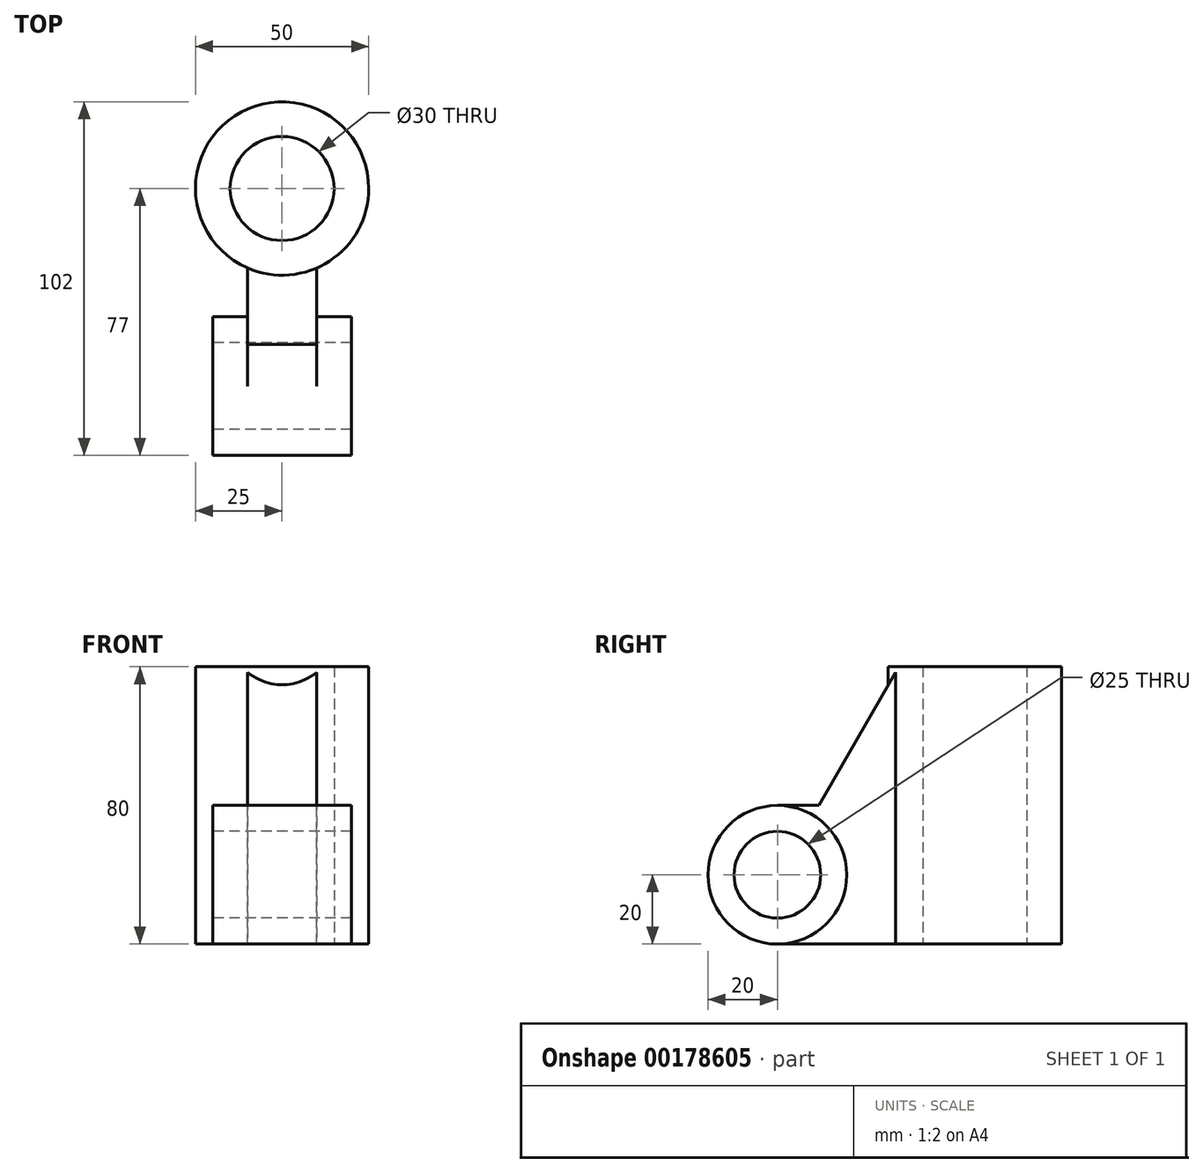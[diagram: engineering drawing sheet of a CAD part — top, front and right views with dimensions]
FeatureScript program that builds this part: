
annotation { "Feature Type Name" : "Feature", "Feature Type Description" : "" }
export const myFeature = defineFeature(function(context is Context, id is Id, definition is map)
    precondition{}
    {
        {
            var Q0;
            Q0=qCreatedBy(makeId("Top.planeOp"),FACE);
            var sketch = newSketch(context, id + "F0", { "sketchPlane" : qUnion([Q0])});
            skCircle(sketch, "E0", {"center": v(0, 0) * mm, "radius": 25 * mm});
            skCircle(sketch, "E1", {"center": v(0, 0) * mm, "radius": 15 * mm});
            skSolve(sketch);
        }
        {
            var Q0;
            Q0 = qSketchRegion(id + "F0", true);
            extrude(context, id + "F1", {"entities" : qUnion([Q0]), "depth" : 80 * mm, "symmetric" : true});
        }
        {
            var Q0;
            Q0=qCreatedBy(makeId("Right.planeOp"),FACE);
            var sketch = newSketch(context, id + "F2", { "sketchPlane" : qUnion([Q0])});
            skCircle(sketch, "E2", {"center": v(-57, -20) * mm, "radius": 20 * mm});
            skLineSegment(sketch, "E3.0", {"start": v(-57, 56.5) * mm, "end": v(-57, -55.51) * mm, "construction": true});
            skCircle(sketch, "E4", {"center": v(-57, -20) * mm, "radius": 12.5 * mm});
            skLineSegment(sketch, "E5", {"start": v(-57, 0) * mm, "end": v(-22, 0) * mm});
            skLineSegment(sketch, "E6.0", {"start": v(-57, -40) * mm, "end": v(-22, -40) * mm});
            skLineSegment(sketch, "E7", {"start": v(-22, 0) * mm, "end": v(-22, -40) * mm});
            skLineSegment(sketch, "E8.0", {"start": v(-45, 56.5) * mm, "end": v(-45, -55.51) * mm, "construction": true});
            skLineSegment(sketch, "E9", {"start": v(0, 40) * mm, "end": v(-66.52, 40) * mm, "construction": true});
            skLineSegment(sketch, "E10", {"start": v(-22, 0) * mm, "end": v(-22, 40) * mm});
            skLineSegment(sketch, "E11", {"start": v(-22, 40) * mm, "end": v(-45, 0) * mm});
            skLineSegment(sketch, "E12", {"start": v(-45, 0) * mm, "end": v(-22, 0) * mm});
            skSolve(sketch);
        }
        {
            var Q0;
            Q0 = qSketchRegion(id + "F2", true);
            extrude(context, id + "F3", {"entities" : qUnion([Q0]), "operationType" : NewBodyOperationType.ADD, "depth" : 20 * mm, "symmetric" : true});
        }
        {
            var Q0;
            Q0=makeQuery(id+"F2.imprint","IMPRINT",FACE,{"disambiguationData":[TD([[makeQuery(id+"F2.imprint","IMPRINT",EDGE,{"derivedFrom":sQuery(id+"F2.wireOp",EDGE,"E4")}),-1.0]])]});
            extrude(context, id + "F4", {"entities" : qUnion([Q0]), "operationType" : NewBodyOperationType.ADD, "depth" : 40 * mm, "symmetric" : true});
        }
    });
